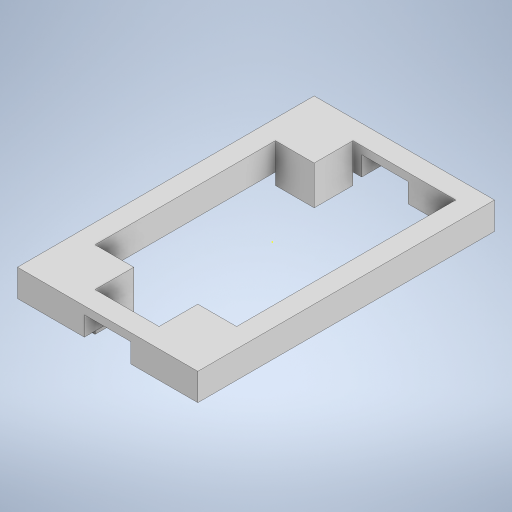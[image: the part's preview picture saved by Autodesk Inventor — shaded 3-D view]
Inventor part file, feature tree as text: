
AUTODESK INVENTOR PART (.ipt)
format: ipt  version: 2024 (Build 280153000, 153)  size: 303,616 bytes
history: native  units: in
note: dims shown in document units (in); Inventor stores cm internally (conversion verified against a paired STEP export)
features: sketch x5, extrude x4
ambient origin geometry x8: Origin, YZ Plane, XZ Plane, XY Plane, X Axis, Y Axis, Z Axis, Center Point
bodies: Solid1 (feature_tree)
feature tree (9):
  extrude  "Extrusion1"  Depth=0.3937in
  sketch  "Sketch2"  dims[d3=0.3937in d4=0.3937in]
  extrude  "Extrusion2"  Depth=0.3937in
  extrude  "Extrusion3"  Depth=0.3937in
  extrude  "Extrusion4"  Depth=0.315in TaperAngle=0.0deg
  sketch  "Sketch1"  dims[d0=0.1969in d1=0.0in d2=0.3937in]
  sketch  "Sketch3"  dims[d5=0.3937in d6=0.3937in]
  sketch  "Sketch4"  dims[d7=0.3937in d8=0.315in d9=0.0in]
  sketch  "Sketch5"  dims[d10=0.0787in d11=0.0in d12=0.0787in d13=0.0in]
